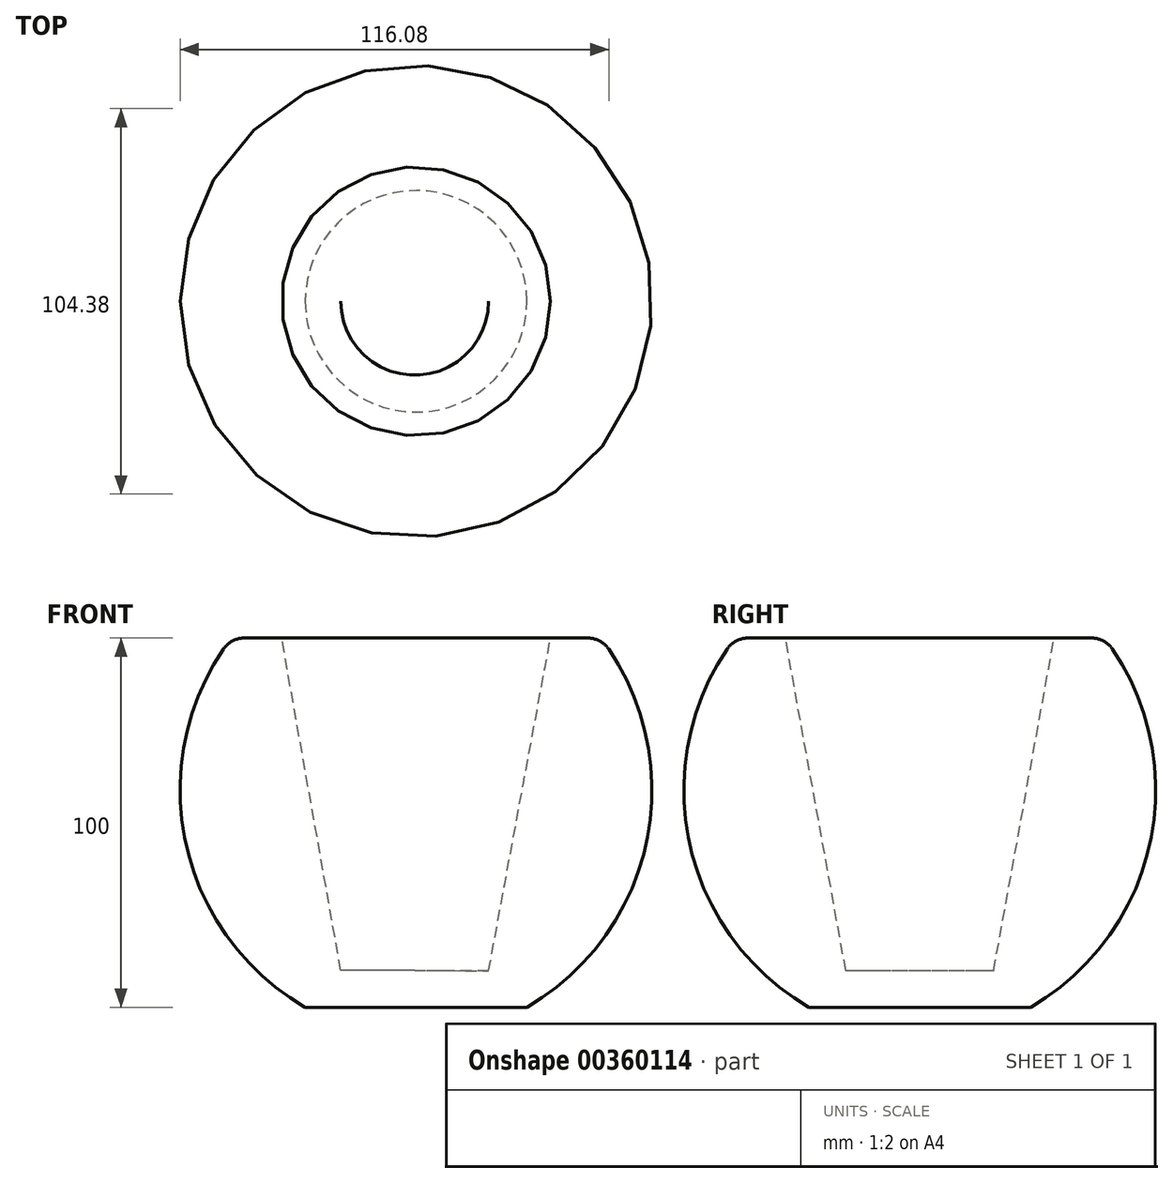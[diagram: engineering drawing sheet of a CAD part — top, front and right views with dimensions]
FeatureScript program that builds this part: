
annotation { "Feature Type Name" : "Feature", "Feature Type Description" : "" }
export const myFeature = defineFeature(function(context is Context, id is Id, definition is map)
    precondition{}
    {
        {
            var Q0;
            Q0=qCreatedBy(makeId("Front.planeOp"),FACE);
            var sketch = newSketch(context, id + "F0", { "sketchPlane" : qUnion([Q0])});
            skLineSegment(sketch, "E0", {"start": v(0, 0) * mm, "end": v(-30, 0) * mm});
            skLineSegment(sketch, "E1", {"start": v(-50, 100) * mm, "end": v(0, 100) * mm});
            skLineSegment(sketch, "E2", {"start": v(0, 100) * mm, "end": v(0, 0) * mm});
            skArc(sketch, "E3", {"start": v(-30, 0) * mm, "mid": v(-62.57, 45.49) * mm, "end": v(-50, 100) * mm});
            skSolve(sketch);
        }
        {
            var Q0;
            Q0=makeQuery(id+"F0.imprint","IMPRINT",FACE,{"disambiguationData":[TD([[makeQuery(id+"F0.imprint","IMPRINT",EDGE,{"derivedFrom":sQuery(id+"F0.wireOp",EDGE,"E0")}),-1.0]])]});
            var Q1;
            Q1=sQuery(id+"F0.wireOp",EDGE,"E2");
            revolve(context, id + "F1", {"entities" : qUnion([Q0]), "axis" : qUnion([Q1]), "revolveType" : RevolveType.FULL});
        }
        {
            var Q0;
            Q0=qCreatedBy(makeId("Front.planeOp"),FACE);
            var sketch = newSketch(context, id + "F2", { "sketchPlane" : qUnion([Q0])});
            skLineSegment(sketch, "E4", {"start": v(-0.35, 10) * mm, "end": v(-20.35, 10) * mm});
            skLineSegment(sketch, "E5", {"start": v(-20.35, 10) * mm, "end": v(-39.94, 120) * mm});
            skLineSegment(sketch, "E6", {"start": v(-39.94, 120) * mm, "end": v(0.06, 120) * mm});
            skLineSegment(sketch, "E7", {"start": v(0.06, 120) * mm, "end": v(-0.35, 10) * mm});
            skSolve(sketch);
        }
        {
            var Q0;
            Q0 = qSketchRegion(id + "F2", true);
            var Q1;
            Q1=sQuery(id+"F2.wireOp",EDGE,"E7");
            revolve(context, id + "F3", {"operationType" : NewBodyOperationType.REMOVE, "entities" : qUnion([Q0]), "axis" : qUnion([Q1]), "revolveType" : RevolveType.FULL, "oppositeDirection" : true});
        }
        {
            var Q0;
            Q0=makeQuery(id+"F1.opRevolve","SWEPT_EDGE",EDGE,{"disambiguationData":[OSD([sQuery(id+"F0.wireOp",EDGE,"HgMkLECc-e3LE-aWRQ-XNub-YSOXlb4UYxY6"),sQuery(id+"F0.wireOp",EDGE,"E1")])]});
            fillet(context, id + "F4", {"entities" : qUnion([Q0]), "radius" : 6.93 * mm, "tangentPropagation" : true, "allowEdgeOverflow" : false});
        }
    });
